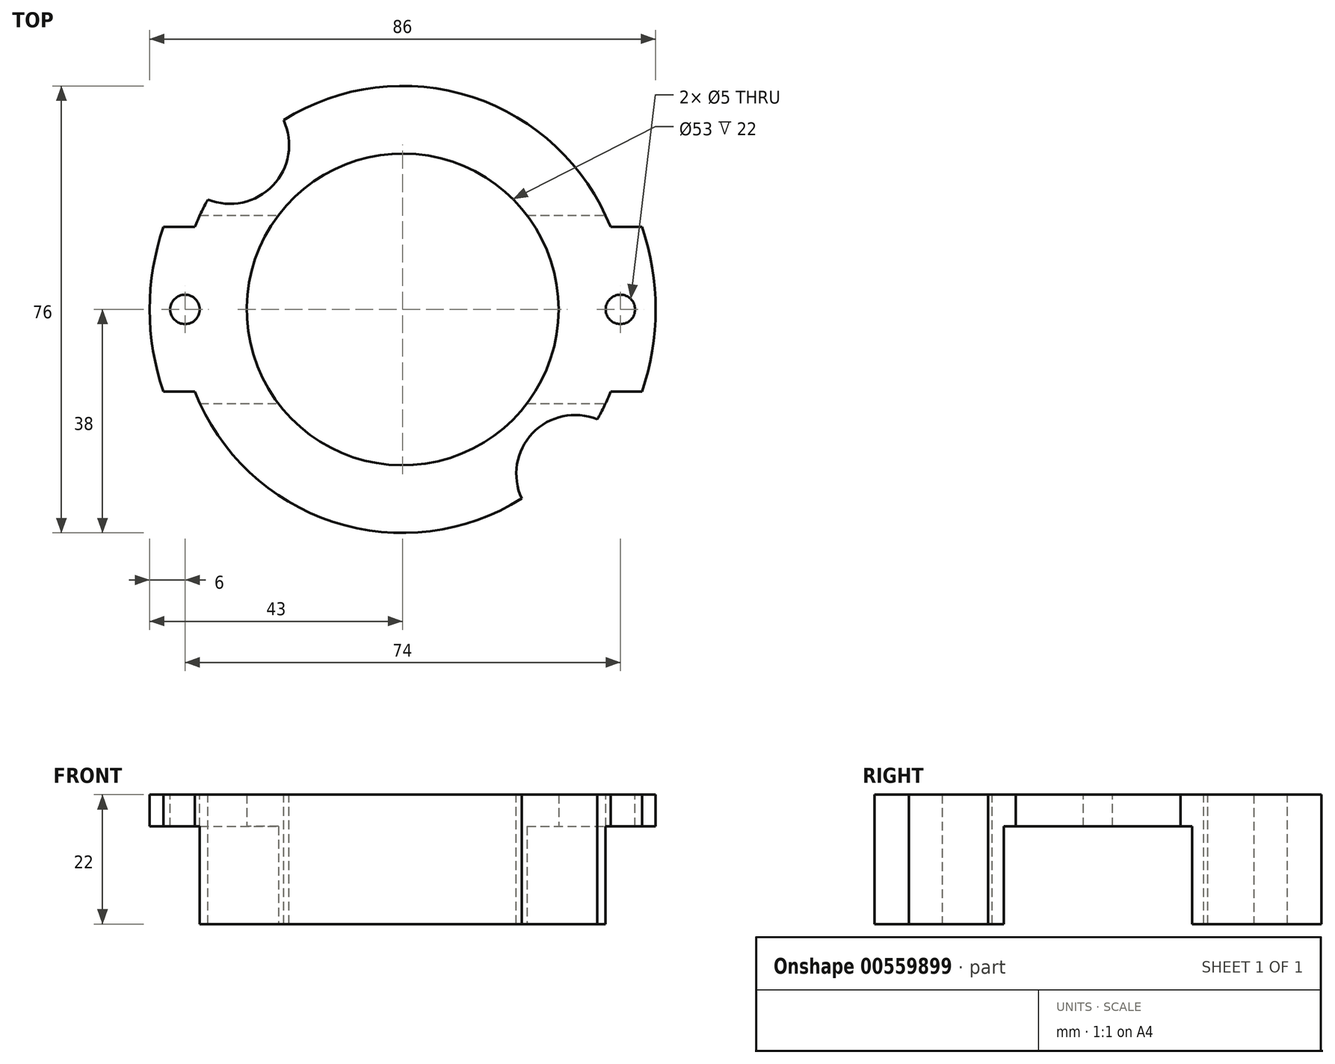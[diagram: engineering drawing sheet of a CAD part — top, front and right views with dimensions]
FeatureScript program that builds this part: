
annotation { "Feature Type Name" : "Feature", "Feature Type Description" : "" }
export const myFeature = defineFeature(function(context is Context, id is Id, definition is map)
    precondition{}
    {
        {
            var Q0;
            Q0=qCreatedBy(makeId("Top.planeOp"),FACE);
            var sketch = newSketch(context, id + "F0", { "sketchPlane" : qUnion([Q0])});
            skCircle(sketch, "E0", {"center": v(0, 0) * mm, "radius": 38 * mm});
            skCircle(sketch, "E1", {"center": v(0, 0) * mm, "radius": 26.5 * mm});
            skSolve(sketch);
        }
        {
            var Q0;
            Q0=makeQuery(id+"F0.imprint","IMPRINT",FACE,{"disambiguationData":[TD([[makeQuery(id+"F0.imprint","IMPRINT",EDGE,{"derivedFrom":sQuery(id+"F0.wireOp",EDGE,"E0")}),1.0]])]});
            extrude(context, id + "F1", {"entities" : qUnion([Q0]), "depth" : 18 * mm, "offsetDistance" : 25 * mm, "hasSecondDirection" : true, "secondDirectionOppositeDirection" : true, "secondDirectionDepth" : 4 * mm});
        }
        {
            var Q0;
            Q0=makeQuery(id+"F1.opExtrude","CAP_FACE",FACE,{"disambiguationData":[OSD([sQuery(id+"F0.wireOp",EDGE,"E0"),sQuery(id+"F0.wireOp",EDGE,"E1")])],"isStart":false});
            var sketch = newSketch(context, id + "F2", { "sketchPlane" : qUnion([Q0])});
            skArc(sketch, "E2", {"start": v(-40.66, 14) * mm, "mid": v(-43, 0) * mm, "end": v(-40.66, -14) * mm});
            skArc(sketch, "E3", {"start": v(-28.22, 14) * mm, "mid": v(-31.5, 0) * mm, "end": v(-28.22, -14) * mm});
            skLineSegment(sketch, "E4", {"start": v(-40.66, 14) * mm, "end": v(-28.22, 14) * mm});
            skLineSegment(sketch, "E5", {"start": v(-40.66, -14) * mm, "end": v(-28.22, -14) * mm});
            skArc(sketch, "E6.trimOffspring", {"start": v(40.66, -14) * mm, "mid": v(43, 0) * mm, "end": v(40.66, 14) * mm});
            skArc(sketch, "E7.trimOffspring", {"start": v(28.22, -14) * mm, "mid": v(31.5, 0) * mm, "end": v(28.22, 14) * mm});
            skLineSegment(sketch, "E8.trimOffspring", {"start": v(28.22, -14) * mm, "end": v(40.66, -14) * mm});
            skLineSegment(sketch, "E9.trimOffspring", {"start": v(28.22, 14) * mm, "end": v(40.66, 14) * mm});
            skSolve(sketch);
        }
        {
            var Q0;
            {var subQ0=sQuery(id+"F2.wireOp",EDGE,"E2");Q0=makeQuery(id+"F2.imprint","IMPRINT",FACE,{"disambiguationData":[TD([[makeQuery(id+"F2.imprint","IMPRINT",EDGE,{"derivedFrom":subQ0}),1.0]])]});}
            var Q1;
            {var subQ0=sQuery(id+"F2.wireOp",EDGE,"E3");Q1=makeQuery(id+"F2.imprint","IMPRINT",FACE,{"disambiguationData":[TD([[makeQuery(id+"F2.imprint","IMPRINT",EDGE,{"derivedFrom":subQ0}),-1.0]])]});}
            var Q2;
            {var subQ0=sQuery(id+"F2.wireOp",EDGE,"E7.trimOffspring");Q2=makeQuery(id+"F2.imprint","IMPRINT",FACE,{"disambiguationData":[TD([[makeQuery(id+"F2.imprint","IMPRINT",EDGE,{"derivedFrom":subQ0}),-1.0]])]});}
            var Q3;
            {var subQ0=sQuery(id+"F2.wireOp",EDGE,"E6.trimOffspring");Q3=makeQuery(id+"F2.imprint","IMPRINT",FACE,{"disambiguationData":[TD([[makeQuery(id+"F2.imprint","IMPRINT",EDGE,{"derivedFrom":subQ0}),1.0]])]});}
            extrude(context, id + "F3", {"entities" : qUnion([Q0, Q1, Q2, Q3]), "operationType" : NewBodyOperationType.ADD, "oppositeDirection" : true, "depth" : 5.4 * mm, "offsetDistance" : 25 * mm});
        }
        {
            var Q0;
            Q0=makeQuery(id+"F3.opExtrude","CAP_FACE",FACE,{"disambiguationData":[OSD([sQuery(id+"F2.wireOp",EDGE,"E6.trimOffspring"),sQuery(id+"F2.wireOp",EDGE,"E7.trimOffspring"),sQuery(id+"F2.wireOp",EDGE,"E8.trimOffspring"),sQuery(id+"F2.wireOp",EDGE,"E9.trimOffspring")])],"isStart":false});
            var sketch = newSketch(context, id + "F4", { "sketchPlane" : qUnion([Q0])});
            skArc(sketch, "E10", {"start": v(-34.47, 16) * mm, "mid": v(-38, 0) * mm, "end": v(-34.47, -16) * mm});
            skArc(sketch, "E11", {"start": v(15.1, -16) * mm, "mid": v(22, 0) * mm, "end": v(15.1, 16) * mm});
            skLineSegment(sketch, "E12", {"start": v(-34.47, 16) * mm, "end": v(-15.1, 16) * mm});
            skLineSegment(sketch, "E13", {"start": v(-34.47, -16) * mm, "end": v(-15.1, -16) * mm});
            skArc(sketch, "E14.trimOffspring", {"start": v(34.47, -16) * mm, "mid": v(38, 0) * mm, "end": v(34.47, 16) * mm});
            skArc(sketch, "E15.trimOffspring", {"start": v(-15.1, 16) * mm, "mid": v(-22, 0) * mm, "end": v(-15.1, -16) * mm});
            skLineSegment(sketch, "E16.trimOffspring", {"start": v(15.1, 16) * mm, "end": v(34.47, 16) * mm});
            skLineSegment(sketch, "E17.trimOffspring", {"start": v(15.1, -16) * mm, "end": v(34.47, -16) * mm});
            skSolve(sketch);
        }
        {
            var Q0;
            Q0=makeQuery(id+"F4.imprint","IMPRINT",FACE,{"disambiguationData":[TD([[makeQuery(id+"F4.imprint","IMPRINT",EDGE,{"derivedFrom":sQuery(id+"F4.wireOp",EDGE,"E10")}),1.0]])]});
            var Q1;
            Q1=makeQuery(id+"F4.imprint","IMPRINT",FACE,{"disambiguationData":[TD([[makeQuery(id+"F4.imprint","IMPRINT",EDGE,{"derivedFrom":sQuery(id+"F4.wireOp",EDGE,"E11")}),-1.0]])]});
            extrude(context, id + "F5", {"entities" : qUnion([Q0, Q1]), "operationType" : NewBodyOperationType.REMOVE, "endBound" : BoundingType.THROUGH_ALL, "depth" : 25 * mm, "offsetDistance" : 25 * mm});
        }
        {
            var Q0;
            Q0=makeQuery(id+"F3.boolean.opBoolean","MERGE",FACE,{"derivedFrom":[makeQuery(id+"F1.opExtrude","CAP_FACE",FACE,{"disambiguationData":[OSD([sQuery(id+"F0.wireOp",EDGE,"E0"),sQuery(id+"F0.wireOp",EDGE,"E1")])],"isStart":false}),makeQuery(id+"F3.opExtrude","CAP_FACE",FACE,{"disambiguationData":[OSD([sQuery(id+"F2.wireOp",EDGE,"E2"),sQuery(id+"F2.wireOp",EDGE,"E3"),sQuery(id+"F2.wireOp",EDGE,"E4"),sQuery(id+"F2.wireOp",EDGE,"E5")])],"isStart":true}),makeQuery(id+"F3.opExtrude","CAP_FACE",FACE,{"disambiguationData":[OSD([sQuery(id+"F2.wireOp",EDGE,"E6.trimOffspring"),sQuery(id+"F2.wireOp",EDGE,"E7.trimOffspring"),sQuery(id+"F2.wireOp",EDGE,"E8.trimOffspring"),sQuery(id+"F2.wireOp",EDGE,"E9.trimOffspring")])],"isStart":true})]});
            var sketch = newSketch(context, id + "F6", { "sketchPlane" : qUnion([Q0])});
            skPoint(sketch, "E18", {"position": v(37, 0) * mm});
            skPoint(sketch, "E19", {"position": v(-37, 0) * mm});
            skPoint(sketch, "E20", {"position": v(-29.3, 27.96) * mm});
            skPoint(sketch, "E21", {"position": v(29.3, -27.96) * mm});
            skLineSegment(sketch, "E22", {"start": v(-29.3, 27.96) * mm, "end": v(0, 0) * mm});
            skLineSegment(sketch, "E23", {"start": v(0, 0) * mm, "end": v(29.3, -27.96) * mm});
            skSolve(sketch);
        }
        {
            var Q0;
            Q0=sQuery(id+"F6.wireOp",VERTEX,"E19");
            var Q1;
            Q1=sQuery(id+"F6.wireOp",VERTEX,"E18");
            var Q2;
            Q2=makeQuery(id+"F1.opExtrude","SWEPT_BODY",BODY,{"disambiguationData":[OSD([sQuery(id+"F0.wireOp",EDGE,"E0"),sQuery(id+"F0.wireOp",EDGE,"E1")])]});
            hole(context, id + "F7", {"style" : HoleStyle.SIMPLE, "endStyle" : HoleEndStyle.THROUGH, "holeDiameter" : 5 * mm, "isTappedThrough" : true, "tappedDepth" : 12 * mm, "tapClearance" : 3, "startFromSketch" : true, "locations" : qUnion([Q0, Q1]), "scope" : qUnion([Q2])});
        }
        {
            var Q0;
            Q0=sQuery(id+"F6.wireOp",VERTEX,"E20");
            var Q1;
            Q1=sQuery(id+"F6.wireOp",VERTEX,"E21");
            var Q2;
            Q2=makeQuery(id+"F1.opExtrude","SWEPT_BODY",BODY,{"disambiguationData":[OSD([sQuery(id+"F0.wireOp",EDGE,"E0"),sQuery(id+"F0.wireOp",EDGE,"E1")])]});
            hole(context, id + "F8", {"style" : HoleStyle.SIMPLE, "endStyle" : HoleEndStyle.THROUGH, "holeDiameter" : 20 * mm, "isTappedThrough" : true, "tappedDepth" : 12 * mm, "tapClearance" : 3, "startFromSketch" : true, "locations" : qUnion([Q0, Q1]), "scope" : qUnion([Q2])});
        }
    });
